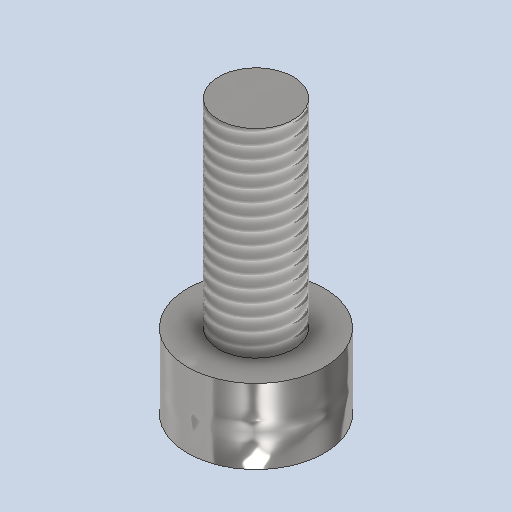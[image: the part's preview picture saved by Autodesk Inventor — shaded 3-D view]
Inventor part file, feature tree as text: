
AUTODESK INVENTOR PART (.ipt)
format: ipt  version: 2024.2 (Build 282272000, 272)  size: 179,200 bytes
history: native  units: mm
features: sketch x2, revolve x1, thread x1, extrude x1
ambient origin geometry x8: Origin, YZ Plane, XZ Plane, XY Plane, X Axis, Y Axis, Z Axis, Center Point
bodies: Solid1 (feature_tree)
feature tree (5):
  revolve  "Revolution1"  [1 undecoded]
  thread  "Thread1"  [1 undecoded]
  extrude  "Extrusion1"  [1 undecoded]
  sketch  "Sketch1"  dims[d4=90.0deg d5=6.0mm d6=0.0mm d0=0.0mm]
  sketch  "Sketch2"
note: 3 required parameter values undecoded (feature->parameter linkage not recoverable at this tier; creation-order binding heuristic only, values carry confidence <= 0.55)